# Revit family: FREGAT LED
name_source: partatom
category: Осветительные приборы
revit_build: Autodesk Revit 2016 (Build: 20150714_1515(x64)
units: mm (PartAtom-declared; Revit-internal decimal feet)

## family parameters
Источник света = Нет
Общий = Нет
Основа = Грань
При загрузке вырезать с полостями = Нет
Размер круглого соединителя = Использовать диаметр
Тип детали = Нормальный
Точка расчета площади = Нет

## types (1)
- FREGAT LED
    ADSK_Единица измерения = Шт.
    ADSK_Завод-изготовитель = ООО МГК Световые технологии
    ADSK_Классификация нагрузок = Прочее
    ADSK_Код изделия = 1426000460
    ADSK_Количество фаз = 1
    ADSK_Количество фаз числовое = 1
    ADSK_Коэффициент мощности = 0.9
    ADSK_Масса = 10.7
    ADSK_Наименование = Серия уличных светильников с уникальной оптической системой, широкой линейкой мощностей, элегантным дизайном, оптимальным сочетанием светотехнических параметров и универсальным поворотным кронштейном. Светильник FREGAT LED является эффективным решением для освещения дорог различных категорий
    ADSK_Напряжение = 230 В
    ADSK_Номинальная мощность = 0 кВт
    ADSK_Полная мощность = 0 кВ·А
    ADSK_Размер_Длина = 722 мм
    ADSK_Размер_Радиус = 70 мм
    ADSK_Размер_Толщина = 91 мм
    ADSK_Размер_Ширина = 265 мм
    ADSK_Ток = 1 А
    ADSK_Энергоэффективность = 91 лм/Вт
    IP Class = IP66
    URL = https://www.ltcompany.com
    r = 10 мм
    Блок аварийного питания = Нет
    Выбор ИС = IES_FREGAT LED : 110 SW 4000K 10000
    Группа модели = Светильники
    Да = Нет
    Изготовитель = ООО МГК Световые технологии
    Излучатель = Плафон самосвечение
    Класс Защиты = I
    Класс пожароопасности = П-ІІІ
    Климатическая зона = УХЛ1
    Код по классификатору = D5020200
    Корпус = Серебристый металл
    Крепление.длина = 150 мм
    Нет = Нет
    Область использования = Автостоянки / парковки, Освещение дорог, Промышленные предприятия, Складские объекты, ТРЦ
    Описание = Серия уличных светильников с уникальной оптической системой, широкой линейкой мощностей, элегантным дизайном, оптимальным сочетанием светотехнических параметров и универсальным поворотным кронштейном. Светильник FREGAT LED является эффективным решением для освещения дорог различных категорий
    Отметка по умолчанию = 0 мм
    Плафон = Плафон прозрачный
    Полная установленная мощность = 0 кВ·А
    Тип ИС = LED
    Тип ПРА = Драйвер
    Тип продукции = Светильник
